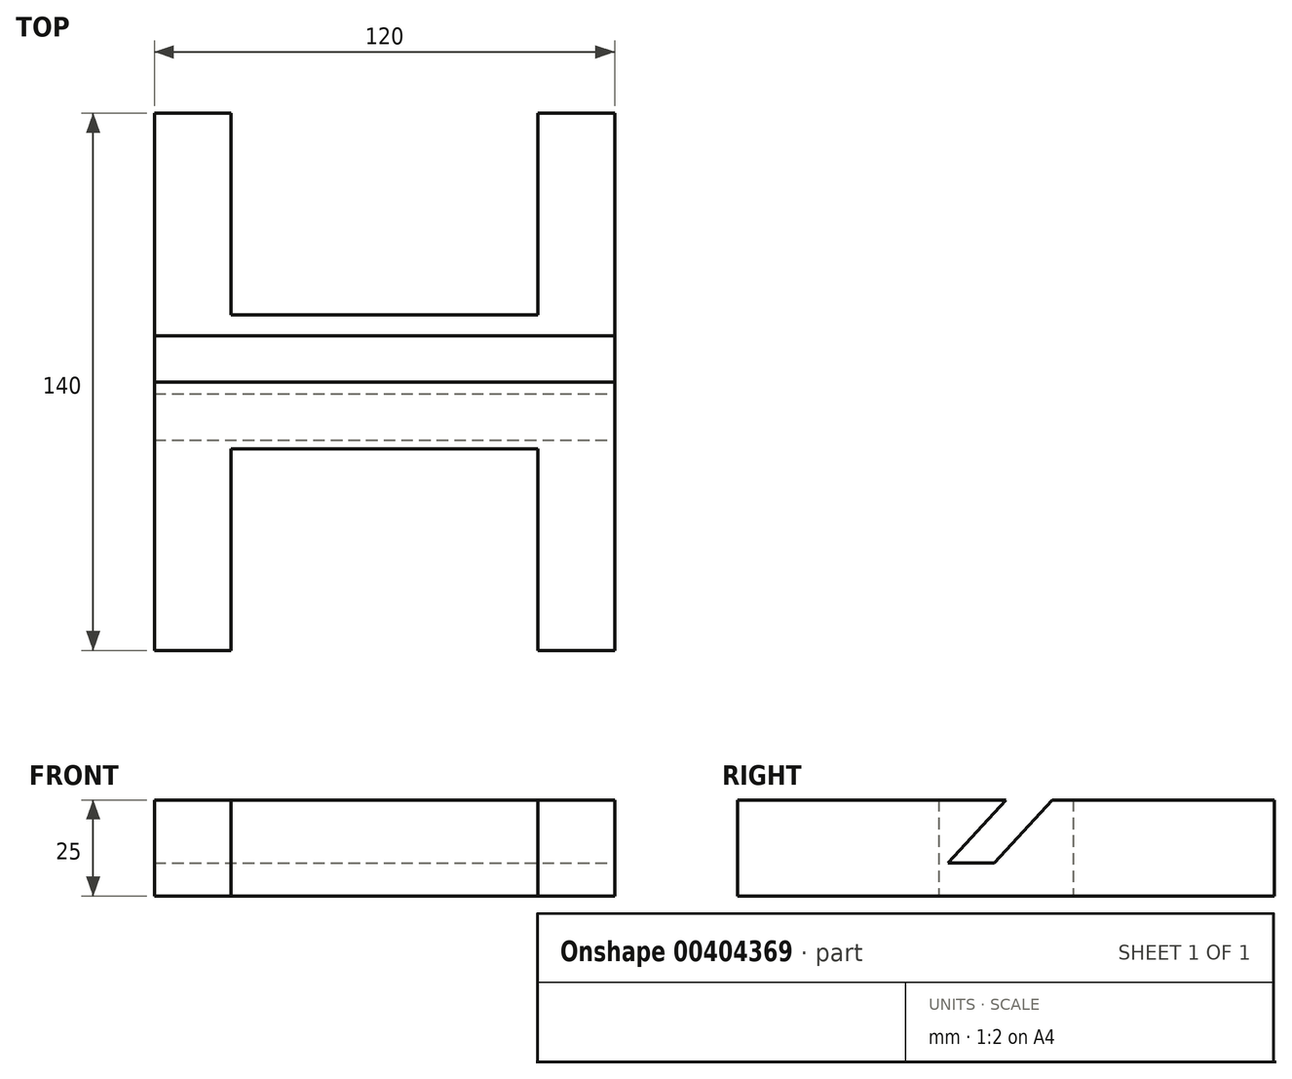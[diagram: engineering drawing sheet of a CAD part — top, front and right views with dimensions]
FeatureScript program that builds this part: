
annotation { "Feature Type Name" : "Feature", "Feature Type Description" : "" }
export const myFeature = defineFeature(function(context is Context, id is Id, definition is map)
    precondition{}
    {
        {
            var Q0;
            Q0=qCreatedBy(makeId("Top.planeOp"),FACE);
            var sketch = newSketch(context, id + "F0", { "sketchPlane" : qUnion([Q0])});
            skLineSegment(sketch, "E0", {"start": v(-40, 70) * mm, "end": v(-60, 70) * mm});
            skLineSegment(sketch, "E1", {"start": v(-60, 70) * mm, "end": v(-60, -70) * mm});
            skLineSegment(sketch, "E2", {"start": v(-60, -70) * mm, "end": v(-40, -70) * mm});
            skLineSegment(sketch, "E3.top", {"start": v(-40, 17.5) * mm, "end": v(0, 17.5) * mm});
            skLineSegment(sketch, "E3.right", {"start": v(0, 4.86) * mm, "end": v(0, 17.5) * mm});
            skLineSegment(sketch, "E4.top", {"start": v(0, -17.5) * mm, "end": v(-40, -17.5) * mm});
            skLineSegment(sketch, "E4.left", {"start": v(0, 4.86) * mm, "end": v(0, -17.5) * mm});
            skLineSegment(sketch, "E5", {"start": v(-40, 17.5) * mm, "end": v(-40, 70) * mm});
            skLineSegment(sketch, "E6", {"start": v(-40, -17.5) * mm, "end": v(-40, -70) * mm});
            skSolve(sketch);
        }
        {
            var Q0;
            Q0 = qSketchRegion(id + "F0", true);
            extrude(context, id + "F1", {"entities" : qUnion([Q0]), "depth" : 25 * mm});
        }
        {
            var Q0;
            Q0=makeQuery(id+"F1.opExtrude","SWEPT_BODY",BODY,{"disambiguationData":[OSD([sQuery(id+"F0.wireOp",EDGE,"E0"),sQuery(id+"F0.wireOp",EDGE,"E1"),sQuery(id+"F0.wireOp",EDGE,"E2"),sQuery(id+"F0.wireOp",EDGE,"E3.top"),sQuery(id+"F0.wireOp",EDGE,"E3.right"),sQuery(id+"F0.wireOp",EDGE,"E4.top"),sQuery(id+"F0.wireOp",EDGE,"E4.left"),sQuery(id+"F0.wireOp",EDGE,"E5"),sQuery(id+"F0.wireOp",EDGE,"E6")])]});
            var Q1;
            Q1=qCreatedBy(makeId("Right.planeOp"),FACE);
            mirror(context, id + "F2", {"operationType" : NewBodyOperationType.ADD, "entities" : qUnion([Q0]), "mirrorPlane" : qUnion([Q1])});
        }
        {
            var Q0;
            Q0=makeQuery(id+"F2.opPattern","COPY",FACE,{"derivedFrom":makeQuery(id+"F1.opExtrude","SWEPT_FACE",FACE,{"disambiguationData":[OSD([sQuery(id+"F0.wireOp",EDGE,"E1")])]}),"instanceName":"1"});
            var sketch = newSketch(context, id + "F3", { "sketchPlane" : qUnion([Q0])});
            skLineSegment(sketch, "E7", {"start": v(0, 25) * mm, "end": v(-15.13, 8.6) * mm});
            skLineSegment(sketch, "E8", {"start": v(-15.13, 8.6) * mm, "end": v(-3.08, 8.6) * mm});
            skLineSegment(sketch, "E9", {"start": v(-3.08, 8.6) * mm, "end": v(12.06, 25) * mm});
            skLineSegment(sketch, "E10", {"start": v(12.06, 25) * mm, "end": v(0, 25) * mm});
            skSolve(sketch);
        }
        {
            var Q0;
            Q0 = qSketchRegion(id + "F3", true);
            extrude(context, id + "F4", {"entities" : qUnion([Q0]), "operationType" : NewBodyOperationType.REMOVE, "oppositeDirection" : true, "depth" : 166.4 * mm});
        }
    });
